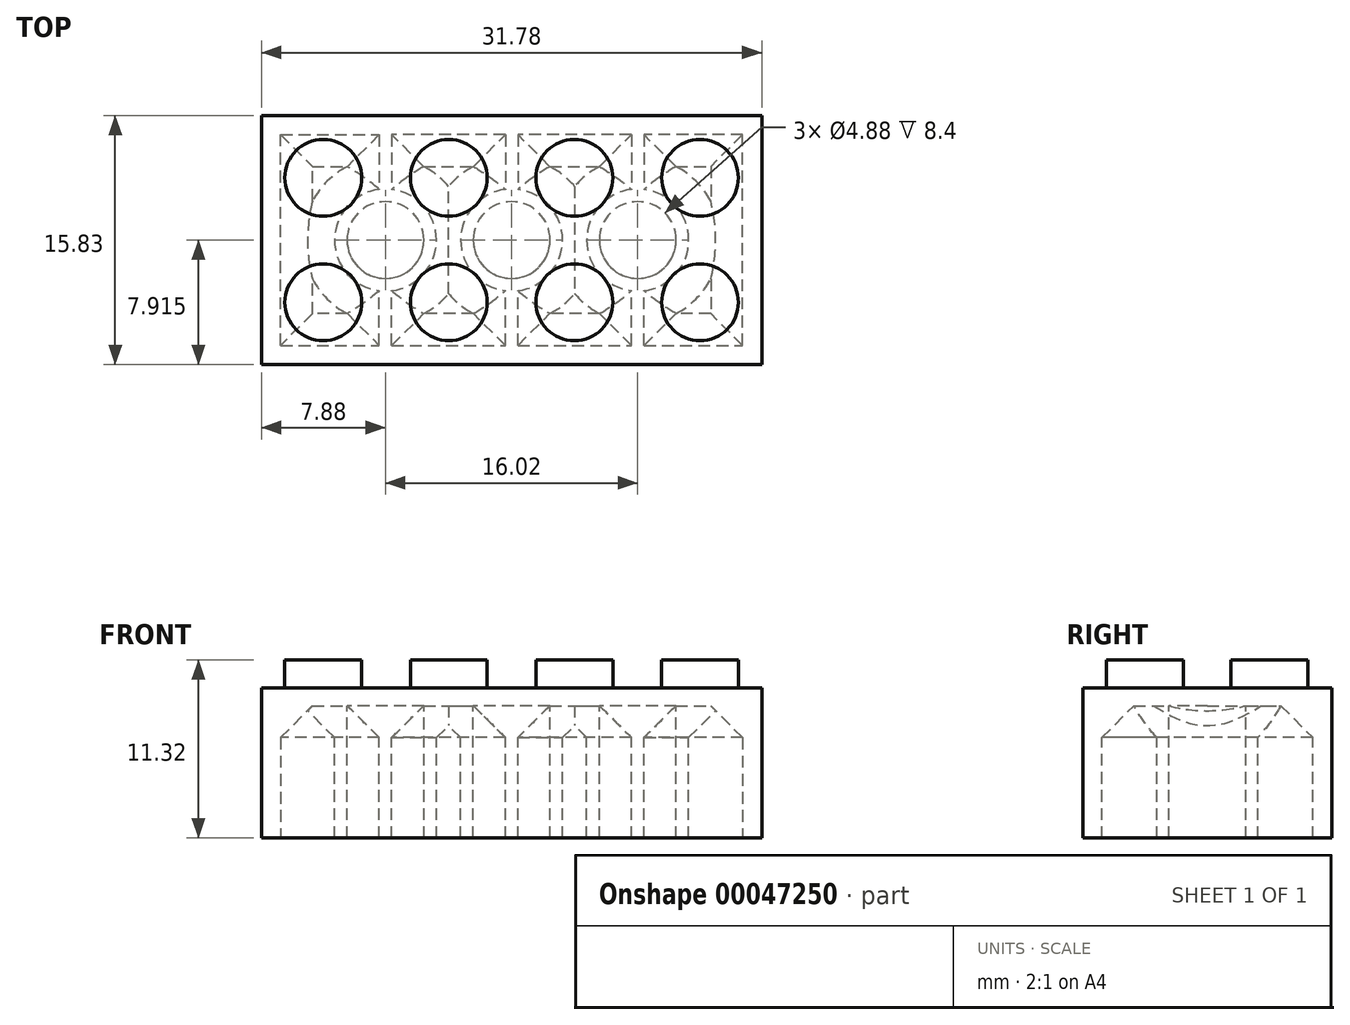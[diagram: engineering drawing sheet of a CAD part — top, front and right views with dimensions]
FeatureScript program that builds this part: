
annotation { "Feature Type Name" : "Feature", "Feature Type Description" : "" }
export const myFeature = defineFeature(function(context is Context, id is Id, definition is map)
    precondition{}
    {
        {
            var Q0;
            Q0=qCreatedBy(makeId("Top.planeOp"),FACE);
            var sketch = newSketch(context, id + "F0", { "sketchPlane" : qUnion([Q0])});
            skLineSegment(sketch, "E0.bottom", {"start": v(0, 0) * mm, "end": v(31.78, 0) * mm});
            skLineSegment(sketch, "E0.top", {"start": v(0, 15.83) * mm, "end": v(31.78, 15.83) * mm});
            skLineSegment(sketch, "E0.left", {"start": v(0, 0) * mm, "end": v(0, 15.83) * mm});
            skLineSegment(sketch, "E0.right", {"start": v(31.78, 0) * mm, "end": v(31.78, 15.83) * mm});
            skSolve(sketch);
        }
        {
            var Q0;
            Q0 = qSketchRegion(id + "F0", true);
            extrude(context, id + "F1", {"entities" : qUnion([Q0]), "depth" : 9.55 * mm});
        }
        {
            var Q0;
            Q0=makeQuery(id+"F1.opExtrude","CAP_FACE",FACE,{"disambiguationData":[OSD([sQuery(id+"F0.wireOp",EDGE,"E0.bottom"),sQuery(id+"F0.wireOp",EDGE,"E0.top"),sQuery(id+"F0.wireOp",EDGE,"E0.left"),sQuery(id+"F0.wireOp",EDGE,"E0.right")])],"isStart":false});
            var sketch = newSketch(context, id + "F2", { "sketchPlane" : qUnion([Q0])});
            skLineSegment(sketch, "E1", {"start": v(15.9, 15.83) * mm, "end": v(15.9, 0) * mm, "construction": true});
            skLineSegment(sketch, "E2", {"start": v(15.9, 0) * mm, "end": v(15.9, 3.96) * mm, "construction": true});
            skLineSegment(sketch, "E3", {"start": v(15.9, 3.96) * mm, "end": v(27.86, 3.96) * mm, "construction": true});
            skCircle(sketch, "E4", {"center": v(27.86, 3.96) * mm, "radius": 2.44 * mm});
            skCircle(sketch, "E5.0.1.0", {"center": v(27.86, 11.87) * mm, "radius": 2.44 * mm});
            skCircle(sketch, "E5.1.0.0", {"center": v(19.88, 3.96) * mm, "radius": 2.44 * mm});
            skCircle(sketch, "E5.1.1.0", {"center": v(19.88, 11.87) * mm, "radius": 2.44 * mm});
            skCircle(sketch, "E5.2.0.0", {"center": v(11.9, 3.96) * mm, "radius": 2.44 * mm});
            skCircle(sketch, "E5.2.1.0", {"center": v(11.9, 11.87) * mm, "radius": 2.44 * mm});
            skCircle(sketch, "E5.3.0.0", {"center": v(3.93, 3.96) * mm, "radius": 2.44 * mm});
            skCircle(sketch, "E5.3.1.0", {"center": v(3.93, 11.87) * mm, "radius": 2.44 * mm});
            skLineSegment(sketch, "E5.direction1", {"start": v(27.86, 3.96) * mm, "end": v(19.88, 3.96) * mm, "construction": true});
            skLineSegment(sketch, "E5.direction2", {"start": v(27.86, 3.96) * mm, "end": v(27.86, 11.87) * mm, "construction": true});
            skLineSegment(sketch, "E6.0", {"start": v(0, 0) * mm, "end": v(0, 15.83) * mm, "construction": true});
            skSolve(sketch);
        }
        {
            var Q0;
            Q0 = qSketchRegion(id + "F2", true);
            extrude(context, id + "F3", {"entities" : qUnion([Q0]), "operationType" : NewBodyOperationType.ADD, "depth" : 1.77 * mm});
        }
        {
            var Q0;
            Q0=makeQuery(id+"F1.opExtrude","CAP_FACE",FACE,{"disambiguationData":[OSD([sQuery(id+"F0.wireOp",EDGE,"E0.bottom"),sQuery(id+"F0.wireOp",EDGE,"E0.top"),sQuery(id+"F0.wireOp",EDGE,"E0.left"),sQuery(id+"F0.wireOp",EDGE,"E0.right")])],"isStart":true});
            var sketch = newSketch(context, id + "F4", { "sketchPlane" : qUnion([Q0])});
            skLineSegment(sketch, "E7.0", {"start": v(0, -15.83) * mm, "end": v(31.78, -15.83) * mm});
            skLineSegment(sketch, "E7.1", {"start": v(0, 0) * mm, "end": v(0, -15.83) * mm});
            skLineSegment(sketch, "E7.2", {"start": v(0, 0) * mm, "end": v(31.78, 0) * mm});
            skLineSegment(sketch, "E7.3", {"start": v(31.78, 0) * mm, "end": v(31.78, -15.83) * mm});
            skLineSegment(sketch, "E8.0", {"start": v(1.22, -14.6) * mm, "end": v(30.56, -14.6) * mm});
            skLineSegment(sketch, "E8.1", {"start": v(1.22, -1.22) * mm, "end": v(1.22, -14.6) * mm});
            skLineSegment(sketch, "E8.2", {"start": v(1.22, -1.22) * mm, "end": v(30.56, -1.22) * mm});
            skLineSegment(sketch, "E8.3", {"start": v(30.56, -1.22) * mm, "end": v(30.56, -14.61) * mm});
            skSolve(sketch);
        }
        {
            var Q0;
            Q0=makeQuery(id+"F4.imprint","IMPRINT",FACE,{"disambiguationData":[TD([[makeQuery(id+"F4.imprint","IMPRINT",EDGE,{"derivedFrom":sQuery(id+"F4.wireOp",EDGE,"E8.0")}),1.0]])]});
            extrude(context, id + "F5", {"entities" : qUnion([Q0]), "operationType" : NewBodyOperationType.REMOVE, "oppositeDirection" : true, "depth" : 8.4 * mm});
        }
        {
            var Q0;
            Q0=makeQuery(id+"F5.boolean.opBoolean","COPY",FACE,{"derivedFrom":makeQuery(id+"F5.opExtrude","CAP_FACE",FACE,{"disambiguationData":[OSD([sQuery(id+"F4.wireOp",EDGE,"E8.0"),sQuery(id+"F4.wireOp",EDGE,"E8.1"),sQuery(id+"F4.wireOp",EDGE,"E8.2"),sQuery(id+"F4.wireOp",EDGE,"E8.3")])],"isStart":false})});
            var sketch = newSketch(context, id + "F6", { "sketchPlane" : qUnion([Q0])});
            skLineSegment(sketch, "E9", {"start": v(15.9, -1.22) * mm, "end": v(15.9, -14.6) * mm, "construction": true});
            skArc(sketch, "E10", {"start": v(15.5, -4.7) * mm, "mid": v(12.65, -7.92) * mm, "end": v(15.5, -11.13) * mm});
            skLineSegment(sketch, "E11", {"start": v(15.9, -7.92) * mm, "end": v(23.9, -7.92) * mm, "construction": true});
            skArc(sketch, "E12", {"start": v(24.3, -11.13) * mm, "mid": v(27.14, -7.91) * mm, "end": v(24.3, -4.7) * mm});
            skArc(sketch, "E13.MirrorC", {"start": v(8.28, -4.7) * mm, "mid": v(11.12, -7.91) * mm, "end": v(8.28, -11.13) * mm});
            skCircle(sketch, "E14", {"center": v(23.9, -7.92) * mm, "radius": 2.44 * mm});
            skCircle(sketch, "E15", {"center": v(15.9, -7.92) * mm, "radius": 2.44 * mm});
            skCircle(sketch, "E16", {"center": v(7.88, -7.91) * mm, "radius": 2.44 * mm});
            skLineSegment(sketch, "E17", {"start": v(15.9, -7.92) * mm, "end": v(16.3, -7.92) * mm});
            skLineSegment(sketch, "E18", {"start": v(15.9, -7.92) * mm, "end": v(15.5, -7.92) * mm, "construction": true});
            skLineSegment(sketch, "E19", {"start": v(15.5, -4.7) * mm, "end": v(15.5, -1.22) * mm});
            skLineSegment(sketch, "E20", {"start": v(15.5, -1.22) * mm, "end": v(16.3, -1.22) * mm});
            skLineSegment(sketch, "E21.trimOffspring", {"start": v(16.3, -4.7) * mm, "end": v(16.3, -1.22) * mm});
            skLineSegment(sketch, "E22.MirrorCS", {"start": v(15.5, -11.13) * mm, "end": v(15.5, -14.6) * mm});
            skLineSegment(sketch, "E23.MirrorCS", {"start": v(15.5, -14.6) * mm, "end": v(16.3, -14.6) * mm});
            skLineSegment(sketch, "E24.MirrorCS", {"start": v(16.3, -11.13) * mm, "end": v(16.3, -14.6) * mm});
            skArc(sketch, "E25.trimOffspring", {"start": v(16.3, -11.13) * mm, "mid": v(19.13, -7.92) * mm, "end": v(16.3, -4.7) * mm});
            skLineSegment(sketch, "E26", {"start": v(19.9, -7.92) * mm, "end": v(19.9, -14.6) * mm, "construction": true});
            skLineSegment(sketch, "E27.MirrorCS", {"start": v(23.5, -11.13) * mm, "end": v(23.5, -14.6) * mm});
            skLineSegment(sketch, "E28.MirrorCS", {"start": v(23.5, -4.7) * mm, "end": v(23.5, -1.22) * mm});
            skLineSegment(sketch, "E29.MirrorCS", {"start": v(23.9, -1.22) * mm, "end": v(23.9, -14.6) * mm, "construction": true});
            skLineSegment(sketch, "E30.MirrorCS", {"start": v(24.3, -4.7) * mm, "end": v(24.3, -1.22) * mm});
            skLineSegment(sketch, "E31.MirrorCS", {"start": v(24.3, -11.13) * mm, "end": v(24.3, -14.6) * mm});
            skLineSegment(sketch, "E32.MirrorCS", {"start": v(24.3, -14.6) * mm, "end": v(23.5, -14.6) * mm});
            skLineSegment(sketch, "E33.MirrorCS", {"start": v(23.9, -7.92) * mm, "end": v(23.5, -7.92) * mm});
            skLineSegment(sketch, "E34.MirrorCS", {"start": v(24.3, -1.22) * mm, "end": v(23.5, -1.22) * mm});
            skLineSegment(sketch, "E35.MirrorCS", {"start": v(23.9, -7.92) * mm, "end": v(24.3, -7.92) * mm, "construction": true});
            skLineSegment(sketch, "E36.MirrorCS", {"start": v(7.48, -14.6) * mm, "end": v(8.28, -14.6) * mm});
            skLineSegment(sketch, "E37.MirrorCS", {"start": v(7.48, -1.22) * mm, "end": v(8.28, -1.22) * mm});
            skLineSegment(sketch, "E38.MirrorCS", {"start": v(8.28, -11.13) * mm, "end": v(8.28, -14.6) * mm});
            skLineSegment(sketch, "E39.MirrorCS", {"start": v(7.88, -1.22) * mm, "end": v(7.88, -14.6) * mm, "construction": true});
            skLineSegment(sketch, "E40.MirrorCS", {"start": v(7.88, -7.92) * mm, "end": v(8.28, -7.92) * mm});
            skLineSegment(sketch, "E41.MirrorCS", {"start": v(7.48, -11.13) * mm, "end": v(7.48, -14.6) * mm});
            skLineSegment(sketch, "E42.MirrorCS", {"start": v(7.88, -7.92) * mm, "end": v(7.48, -7.92) * mm, "construction": true});
            skLineSegment(sketch, "E43.MirrorCS", {"start": v(8.28, -4.7) * mm, "end": v(8.28, -1.22) * mm});
            skLineSegment(sketch, "E44.MirrorCS", {"start": v(7.48, -4.7) * mm, "end": v(7.48, -1.22) * mm});
            skArc(sketch, "E45.trimOffspring", {"start": v(7.48, -11.13) * mm, "mid": v(4.64, -7.91) * mm, "end": v(7.48, -4.7) * mm});
            skArc(sketch, "E46.trimOffspring", {"start": v(23.5, -4.7) * mm, "mid": v(20.66, -7.91) * mm, "end": v(23.5, -11.13) * mm});
            skSolve(sketch);
        }
        {
            var Q0;
            Q0 = qSketchRegion(id + "F6", true);
            var Q1;
            Q1=makeQuery(id+"F1.opExtrude","CAP_FACE",FACE,{"disambiguationData":[OSD([sQuery(id+"F0.wireOp",EDGE,"E0.bottom"),sQuery(id+"F0.wireOp",EDGE,"E0.top"),sQuery(id+"F0.wireOp",EDGE,"E0.left"),sQuery(id+"F0.wireOp",EDGE,"E0.right")])],"isStart":true});
            extrude(context, id + "F7", {"entities" : qUnion([Q0]), "operationType" : NewBodyOperationType.ADD, "endBound" : BoundingType.UP_TO_SURFACE, "endBoundEntityFace" : qUnion([Q1]), "depth" : 25 * mm});
        }
        {
            var Q0;
            {var subQ0=sQuery(id+"F4.wireOp",EDGE,"E8.3");var subQ1=sQuery(id+"F4.wireOp",EDGE,"E8.2");var subQ2=sQuery(id+"F4.wireOp",EDGE,"E8.1");var subQ3=sQuery(id+"F4.wireOp",EDGE,"E8.0");Q0=makeQuery(id+"F7.boolean.opBoolean","SPLIT",FACE,{"disambiguationData":[TD([makeQuery(id+"F5.boolean.opBoolean","COPY",FACE,{"derivedFrom":makeQuery(id+"F5.opExtrude","SWEPT_FACE",FACE,{"disambiguationData":[OSD([subQ3])]})})])],"derivedFrom":makeQuery(id+"F5.boolean.opBoolean","COPY",FACE,{"derivedFrom":makeQuery(id+"F5.opExtrude","CAP_FACE",FACE,{"disambiguationData":[OSD([subQ3,subQ2,subQ1,subQ0])],"isStart":false})})});}
            var Q1;
            {var subQ0=sQuery(id+"F4.wireOp",EDGE,"E8.2");var subQ1=sQuery(id+"F4.wireOp",EDGE,"E8.0");Q1=makeQuery(id+"F7.boolean.opBoolean","SPLIT",FACE,{"disambiguationData":[TD([makeQuery(id+"F7.opExtrude","SWEPT_FACE",FACE,{"disambiguationData":[OSD([sQuery(id+"F6.wireOp",EDGE,"E10")])]})])],"derivedFrom":makeQuery(id+"F5.boolean.opBoolean","COPY",FACE,{"derivedFrom":makeQuery(id+"F5.opExtrude","CAP_FACE",FACE,{"disambiguationData":[OSD([subQ1,sQuery(id+"F4.wireOp",EDGE,"E8.1"),subQ0,sQuery(id+"F4.wireOp",EDGE,"E8.3")])],"isStart":false})})});}
            var Q2;
            {var subQ0=sQuery(id+"F4.wireOp",EDGE,"E8.2");var subQ1=sQuery(id+"F4.wireOp",EDGE,"E8.0");Q2=makeQuery(id+"F7.boolean.opBoolean","SPLIT",FACE,{"disambiguationData":[TD([makeQuery(id+"F7.opExtrude","SWEPT_FACE",FACE,{"disambiguationData":[OSD([sQuery(id+"F6.wireOp",EDGE,"E21.trimOffspring")])]})])],"derivedFrom":makeQuery(id+"F5.boolean.opBoolean","COPY",FACE,{"derivedFrom":makeQuery(id+"F5.opExtrude","CAP_FACE",FACE,{"disambiguationData":[OSD([subQ1,sQuery(id+"F4.wireOp",EDGE,"E8.1"),subQ0,sQuery(id+"F4.wireOp",EDGE,"E8.3")])],"isStart":false})})});}
            chamfer(context, id + "F8", {"entities" : qUnion([Q0, Q1, Q2]), "width" : 2.02 * mm, "tangentPropagation" : true});
        }
    });
